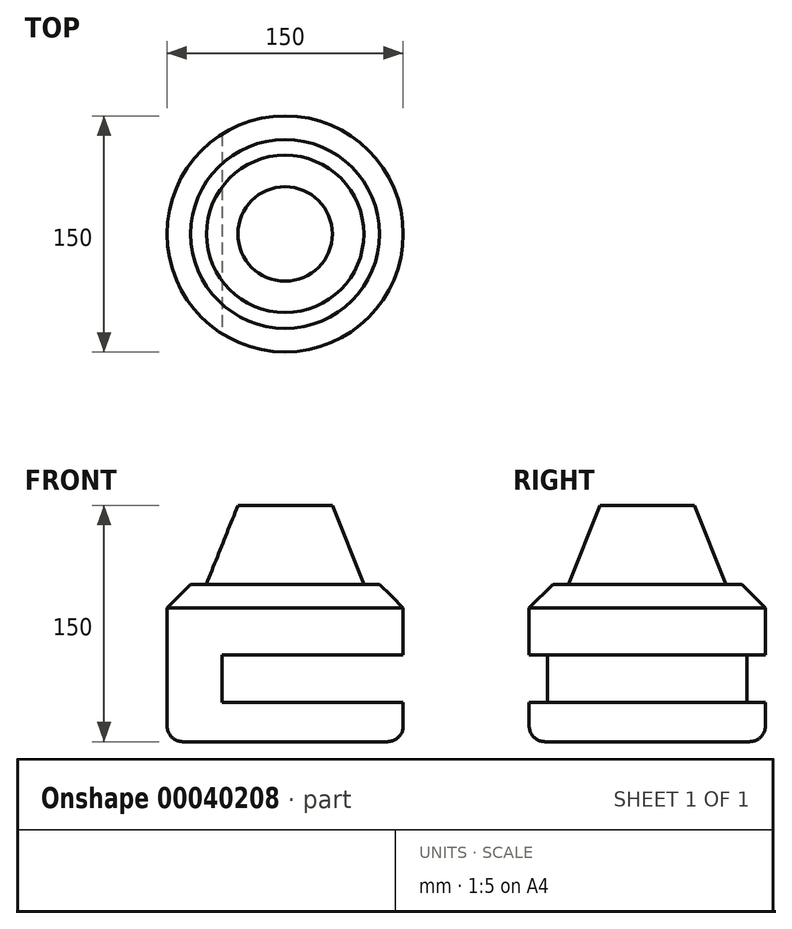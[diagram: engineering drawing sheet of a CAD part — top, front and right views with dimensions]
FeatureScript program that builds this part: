
annotation { "Feature Type Name" : "Feature", "Feature Type Description" : "" }
export const myFeature = defineFeature(function(context is Context, id is Id, definition is map)
    precondition{}
    {
        {
            var Q0;
            Q0=qCreatedBy(makeId("Top.planeOp"),FACE);
            var sketch = newSketch(context, id + "F0", { "sketchPlane" : qUnion([Q0])});
            skCircle(sketch, "E0", {"center": v(0, 0) * mm, "radius": 75 * mm});
            skSolve(sketch);
        }
        {
            var Q0;
            Q0=makeQuery(id+"F0.imprint","IMPRINT",FACE,{"disambiguationData":[TD([[makeQuery(id+"F0.imprint","IMPRINT",EDGE,{"derivedFrom":sQuery(id+"F0.wireOp",EDGE,"E0")}),1.0]])]});
            extrude(context, id + "F1", {"entities" : qUnion([Q0]), "depth" : 100 * mm});
        }
        {
            var Q0;
            Q0=makeQuery(id+"F1.opExtrude","CAP_EDGE",EDGE,{"disambiguationData":[OSD([sQuery(id+"F0.wireOp",EDGE,"E0")])],"isStart":true});
            fillet(context, id + "F2", {"entities" : qUnion([Q0]), "radius" : 10 * mm, "tangentPropagation" : true, "allowEdgeOverflow" : false});
        }
        {
            var Q0;
            Q0=makeQuery(id+"F1.opExtrude","CAP_EDGE",EDGE,{"disambiguationData":[OSD([sQuery(id+"F0.wireOp",EDGE,"E0")])],"isStart":false});
            chamfer(context, id + "F3", {"entities" : qUnion([Q0]), "width" : 15 * mm, "tangentPropagation" : true});
        }
        {
            var Q0;
            Q0=qCreatedBy(makeId("Front.planeOp"),FACE);
            var sketch = newSketch(context, id + "F4", { "sketchPlane" : qUnion([Q0])});
            skLineSegment(sketch, "E1.bottom", {"start": v(-40, 55) * mm, "end": v(110, 55) * mm});
            skLineSegment(sketch, "E1.top", {"start": v(-40, 25) * mm, "end": v(110, 25) * mm});
            skLineSegment(sketch, "E1.left", {"start": v(-40, 55) * mm, "end": v(-40, 25) * mm});
            skLineSegment(sketch, "E1.right", {"start": v(110, 55) * mm, "end": v(110, 25) * mm});
            skSolve(sketch);
        }
        {
            var Q0;
            Q0=makeQuery(id+"F4.imprint","IMPRINT",FACE,{"disambiguationData":[TD([[makeQuery(id+"F4.imprint","IMPRINT",EDGE,{"derivedFrom":sQuery(id+"F4.wireOp",EDGE,"E1.bottom")}),-1.0]])]});
            extrude(context, id + "F5", {"entities" : qUnion([Q0]), "operationType" : NewBodyOperationType.REMOVE, "endBound" : BoundingType.SYMMETRIC, "oppositeDirection" : true, "depth" : 250 * mm});
        }
        {
            var Q0;
            Q0=qCreatedBy(makeId("Front.planeOp"),FACE);
            var sketch = newSketch(context, id + "F6", { "sketchPlane" : qUnion([Q0])});
            skLineSegment(sketch, "E2", {"start": v(0, 100) * mm, "end": v(0, 150) * mm});
            skLineSegment(sketch, "E3", {"start": v(0, 150) * mm, "end": v(30, 150) * mm});
            skLineSegment(sketch, "E4", {"start": v(30, 150) * mm, "end": v(50, 100) * mm});
            skLineSegment(sketch, "E5", {"start": v(50, 100) * mm, "end": v(0, 100) * mm});
            skSolve(sketch);
        }
        {
            var Q0;
            Q0=makeQuery(id+"F6.imprint","IMPRINT",FACE,{"disambiguationData":[TD([[makeQuery(id+"F6.imprint","IMPRINT",EDGE,{"derivedFrom":sQuery(id+"F6.wireOp",EDGE,"E2")}),-1.0]])]});
            var Q1;
            Q1=sQuery(id+"F6.wireOp",EDGE,"E2");
            revolve(context, id + "F7", {"operationType" : NewBodyOperationType.ADD, "entities" : qUnion([Q0]), "axis" : qUnion([Q1]), "revolveType" : RevolveType.FULL});
        }
    });
